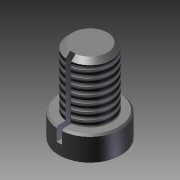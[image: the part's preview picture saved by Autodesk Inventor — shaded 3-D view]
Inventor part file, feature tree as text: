
AUTODESK INVENTOR PART (.ipt)
format: ipt  version: 2015 (Build 190159000, 159)  size: 135,680 bytes
history: native  units: in
note: dims shown in document units (in); Inventor stores cm internally (conversion verified against a paired STEP export)
features: other x49, sketch x2, revolve x1, thread x1, extrude x1
ambient origin geometry x8: Origin, YZ Plane, XZ Plane, XY Plane, X Axis, Y Axis, Z Axis, Center Point
bodies: Solid1 (feature_tree)
feature tree (54):
  revolve  "Revolution1"  [1 undecoded]
  thread  "Thread1"  [1 undecoded]
  extrude  "Extrusion1"  [1 undecoded]
  other  "at507_XY"
  other  "at507_YZ"
  other  "at507_ZX"
  other  "at507_X"
  other  "at507_Y"
  other  "at507_Z"
  other  "at507_Center"
  other  "at513_XY"
  other  "at513_YZ"
  other  "at513_ZX"
  other  "at513_X"
  other  "at513_Y"
  other  "at513_Z"
  other  "at513_Center"
  other  "at516_XY"
  other  "at516_YZ"
  other  "at516_ZX"
  other  "at516_X"
  other  "at516_Y"
  other  "at516_Z"
  other  "at516_Center"
  other  "to_at509_XY"
  other  "to_at509_YZ"
  other  "to_at509_ZX"
  other  "to_at509_X"
  other  "to_at509_Y"
  other  "to_at509_Z"
  other  "to_at509_Center"
  other  "to_at513_1_XY"
  other  "to_at513_1_YZ"
  other  "to_at513_1_ZX"
  other  "to_at513_1_X"
  other  "to_at513_1_Y"
  other  "to_at513_1_Z"
  other  "to_at513_1_Center"
  other  "to_bodycover_XY"
  other  "to_bodycover_YZ"
  other  "to_bodycover_ZX"
  other  "to_bodycover_X"
  other  "to_bodycover_Y"
  other  "to_bodycover_Z"
  other  "to_bodycover_Center"
  other  "to_plunger_XY"
  other  "to_plunger_YZ"
  other  "to_plunger_ZX"
  other  "to_plunger_X"
  other  "to_plunger_Y"
  other  "to_plunger_Z"
  other  "to_plunger_Center"
  sketch  "Sketch_1"  dims[d0=360.0deg d1=0.3096in d2=0.0in d3=0.48in d4=0.0in]
  sketch  "Sketch_3"
note: 3 required parameter values undecoded (feature->parameter linkage not recoverable at this tier; creation-order binding heuristic only, values carry confidence <= 0.55)